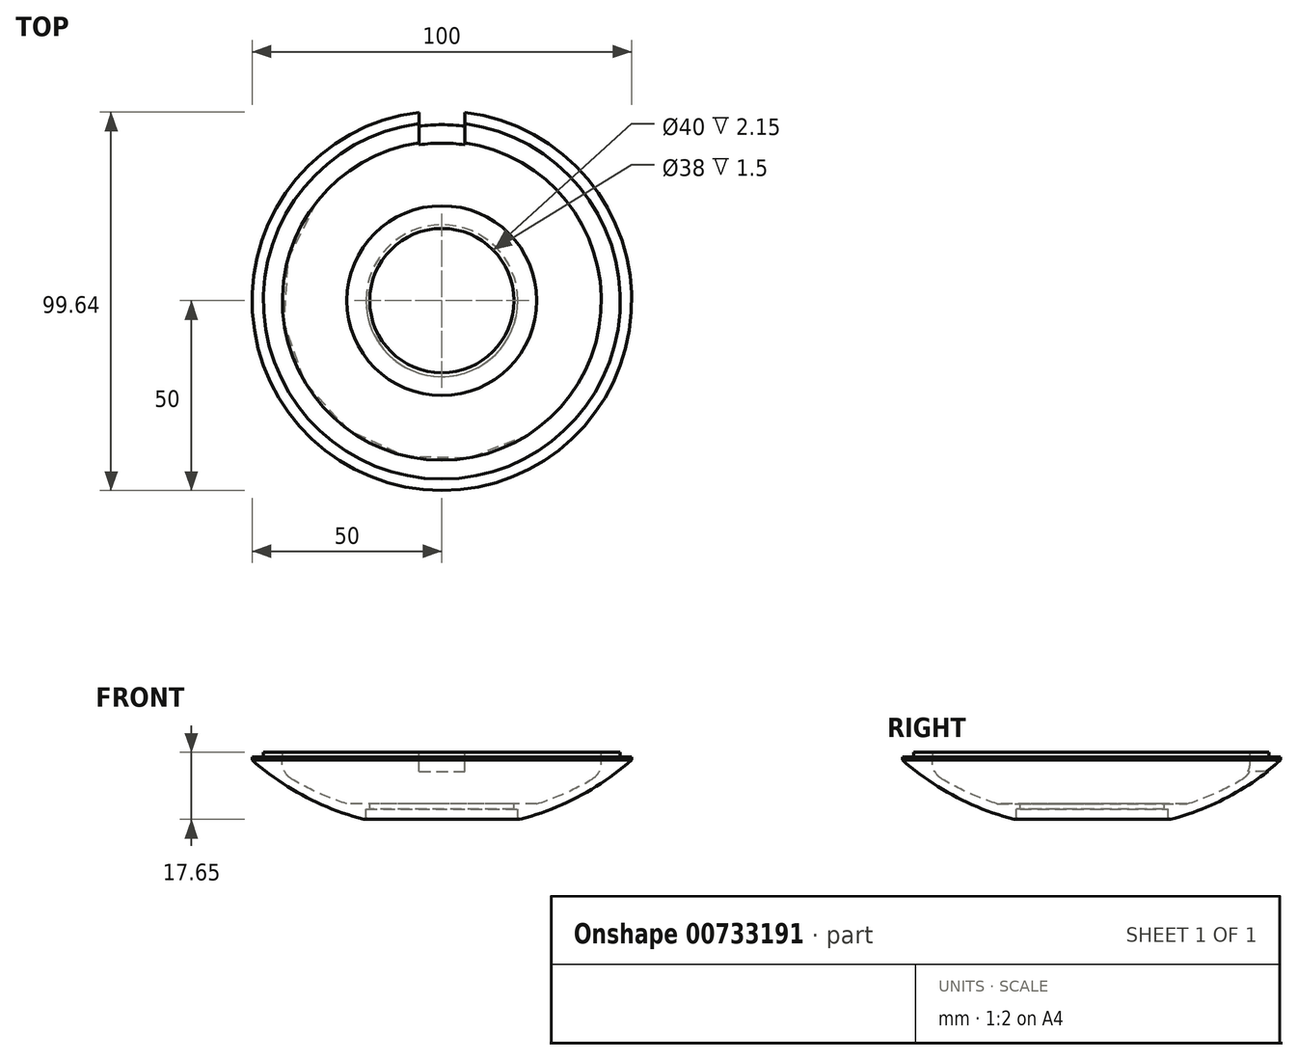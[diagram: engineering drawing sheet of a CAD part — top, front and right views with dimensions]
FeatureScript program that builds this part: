
annotation { "Feature Type Name" : "Feature", "Feature Type Description" : "" }
export const myFeature = defineFeature(function(context is Context, id is Id, definition is map)
    precondition{}
    {
        {
            var Q0;
            Q0=qCreatedBy(makeId("Right.planeOp"),FACE);
            var sketch = newSketch(context, id + "F0", { "sketchPlane" : qUnion([Q0])});
            skArc(sketch, "E0", {"start": v(-47, 0) * mm, "mid": v(-24.82, -11.62) * mm, "end": v(0, -15) * mm});
            skLineSegment(sketch, "E1", {"start": v(-47, 0) * mm, "end": v(-42, 0) * mm});
            skLineSegment(sketch, "E2", {"start": v(-42, 0) * mm, "end": v(-42, 2) * mm});
            skLineSegment(sketch, "E3", {"start": v(-42, 2) * mm, "end": v(-47, 2) * mm});
            skLineSegment(sketch, "E4", {"start": v(-47, 2) * mm, "end": v(-47, 3.7) * mm});
            skLineSegment(sketch, "E5", {"start": v(-47, 3.7) * mm, "end": v(-42, 3.7) * mm});
            skLineSegment(sketch, "E6", {"start": v(-42, 3.7) * mm, "end": v(-42, 5.7) * mm});
            skLineSegment(sketch, "E7", {"start": v(-45, 5.7) * mm, "end": v(-50, 5.7) * mm});
            skLineSegment(sketch, "E8", {"start": v(-50, 5.7) * mm, "end": v(-50, 0) * mm});
            skArc(sketch, "E9", {"start": v(-50, 0) * mm, "mid": v(-26.7, -13.74) * mm, "end": v(0, -18) * mm});
            skLineSegment(sketch, "E10", {"start": v(0, -15) * mm, "end": v(0, -18) * mm});
            skLineSegment(sketch, "E11", {"start": v(0, 0) * mm, "end": v(0, -18) * mm, "construction": true});
            skArc(sketch, "E12", {"start": v(-11, 19.5) * mm, "mid": v(-27.35, 14.5) * mm, "end": v(-42, 5.7) * mm});
            skArc(sketch, "E13", {"start": v(-14, 21.9) * mm, "mid": v(-30.58, 15.86) * mm, "end": v(-45, 5.7) * mm});
            skLineSegment(sketch, "E14", {"start": v(0, 33) * mm, "end": v(0, 36) * mm});
            skArc(sketch, "E15", {"start": v(0, 36) * mm, "mid": v(-9.93, 31.87) * mm, "end": v(-14, 21.9) * mm});
            skArc(sketch, "E16", {"start": v(0, 33) * mm, "mid": v(-7.92, 30.29) * mm, "end": v(-11, 22.5) * mm});
            skLineSegment(sketch, "E17", {"start": v(-11, 22.5) * mm, "end": v(-2.5, 22.5) * mm});
            skLineSegment(sketch, "E18", {"start": v(-11, 19.5) * mm, "end": v(-2.5, 19.5) * mm});
            skLineSegment(sketch, "E19", {"start": v(-2.5, 22.5) * mm, "end": v(-2.5, 19.5) * mm});
            skLineSegment(sketch, "E20", {"start": v(-47, 2) * mm, "end": v(-47, 0.8) * mm});
            skLineSegment(sketch, "E21", {"start": v(-47, 0.8) * mm, "end": v(-50, 0.8) * mm});
            skSolve(sketch);
        }
        {
            var Q0;
            Q0=makeQuery(id+"F0.imprint","IMPRINT",FACE,{"disambiguationData":[TD([[makeQuery(id+"F0.imprint","IMPRINT",EDGE,{"derivedFrom":sQuery(id+"F0.wireOp",EDGE,"E0")}),-1.0]])]});
            var Q1;
            Q1=sQuery(id+"F0.wireOp",EDGE,"E11");
            revolve(context, id + "F1", {"surfaceOperationType" : NewSurfaceOperationType.NEW, "entities" : qUnion([Q0]), "axis" : qUnion([Q1]), "revolveType" : RevolveType.ONE_DIRECTION, "angle" : 360 * degree});
        }
        {
            var Q0;
            Q0=qCreatedBy(makeId("Top.planeOp"),FACE);
            var sketch = newSketch(context, id + "F2", { "sketchPlane" : qUnion([Q0])});
            skCircle(sketch, "E22", {"center": v(0, 0) * mm, "radius": 20 * mm});
            skSolve(sketch);
        }
        {
            var Q0;
            Q0=makeQuery(id+"F2.imprint","IMPRINT",FACE,{"disambiguationData":[TD([[makeQuery(id+"F2.imprint","IMPRINT",EDGE,{"derivedFrom":sQuery(id+"F2.wireOp",EDGE,"E22")}),1.0]])]});
            extrude(context, id + "F3", {"entities" : qUnion([Q0]), "operationType" : NewBodyOperationType.REMOVE, "oppositeDirection" : true, "depth" : 25 * mm, "offsetDistance" : 25 * mm});
        }
        {
            var Q0;
            Q0=qCreatedBy(makeId("Top.planeOp"),FACE);
            var sketch = newSketch(context, id + "F4", { "sketchPlane" : qUnion([Q0])});
            skCircle(sketch, "E23", {"center": v(0, -26) * mm, "radius": 2.5 * mm});
            skCircle(sketch, "E24", {"center": v(-22.52, 13) * mm, "radius": 2.5 * mm});
            skLineSegment(sketch, "E25", {"start": v(0, 0) * mm, "end": v(-22.52, 13) * mm, "construction": true});
            skCircle(sketch, "E26.MirrorC", {"center": v(22.52, 13) * mm, "radius": 2.5 * mm});
            skSolve(sketch);
        }
        {
            var Q0;
            Q0=makeQuery(id+"F4.imprint","IMPRINT",FACE,{"disambiguationData":[TD([[makeQuery(id+"F4.imprint","IMPRINT",EDGE,{"derivedFrom":sQuery(id+"F4.wireOp",EDGE,"E23")}),1.0]])]});
            var Q1;
            Q1=makeQuery(id+"F4.imprint","IMPRINT",FACE,{"disambiguationData":[TD([[makeQuery(id+"F4.imprint","IMPRINT",EDGE,{"derivedFrom":sQuery(id+"F4.wireOp",EDGE,"E24")}),1.0]])]});
            var Q2;
            Q2=makeQuery(id+"F4.imprint","IMPRINT",FACE,{"disambiguationData":[TD([[makeQuery(id+"F4.imprint","IMPRINT",EDGE,{"derivedFrom":sQuery(id+"F4.wireOp",EDGE,"E26.MirrorC")}),-1.0]])]});
            extrude(context, id + "F5", {"entities" : qUnion([Q0, Q1, Q2]), "operationType" : NewBodyOperationType.REMOVE, "depth" : 25 * mm, "offsetDistance" : 25 * mm});
        }
        {
            var Q0;
            Q0=makeQuery(id+"F1.opRevolve","SWEPT_EDGE",EDGE,{"disambiguationData":[OSD([sQuery(id+"F0.wireOp",EDGE,"E0"),sQuery(id+"F0.wireOp",EDGE,"E1")])]});
            var Q1;
            Q1=makeQuery(id+"F1.opRevolve","SWEPT_EDGE",EDGE,{"disambiguationData":[OSD([sQuery(id+"F0.wireOp",EDGE,"E6"),sQuery(id+"F0.wireOp",EDGE,"E12")])]});
            fillet(context, id + "F6", {"entities" : qUnion([Q0, Q1]), "radius" : 5 * mm, "tangentPropagation" : true, "allowEdgeOverflow" : false});
        }
        {
            var Q0;
            Q0=qCreatedBy(makeId("Front.planeOp"),FACE);
            var sketch = newSketch(context, id + "F7", { "sketchPlane" : qUnion([Q0])});
            skLineSegment(sketch, "E27.bottom", {"start": v(-6, 3.6) * mm, "end": v(6, 3.6) * mm});
            skLineSegment(sketch, "E27.top", {"start": v(-6, -3) * mm, "end": v(6, -3) * mm});
            skLineSegment(sketch, "E27.left", {"start": v(-6, 3.6) * mm, "end": v(-6, -3) * mm});
            skLineSegment(sketch, "E27.right", {"start": v(6, 3.6) * mm, "end": v(6, -3) * mm});
            skPoint(sketch, "E28.right.end.orphan", {"position": v(5, 0) * mm});
            skSolve(sketch);
        }
        {
            var Q0;
            Q0=makeQuery(id+"F7.imprint","IMPRINT",FACE,{"disambiguationData":[TD([[makeQuery(id+"F7.imprint","IMPRINT",EDGE,{"derivedFrom":sQuery(id+"F7.wireOp",EDGE,"PHSBLFIY-TZuw-bhm2-DLcI-erlKNIHIbNUr.bottom")}),-1.0]])]});
            var Q1;
            Q1=makeQuery(id+"F7.imprint","IMPRINT",FACE,{"disambiguationData":[TD([[makeQuery(id+"F7.imprint","IMPRINT",EDGE,{"derivedFrom":sQuery(id+"F7.wireOp",EDGE,"PHSBLFIY-TZuw-bhm2-DLcI-erlKNIHIbNUr.right")}),-1.0]])]});
            var Q2;
            Q2=makeQuery(id+"F7.imprint","IMPRINT",FACE,{"disambiguationData":[TD([[makeQuery(id+"F7.imprint","IMPRINT",EDGE,{"derivedFrom":sQuery(id+"F7.wireOp",EDGE,"E27.bottom")}),-1.0]])]});
            extrude(context, id + "F8", {"entities" : qUnion([Q0, Q1, Q2]), "operationType" : NewBodyOperationType.REMOVE, "oppositeDirection" : true, "depth" : 60 * mm, "offsetDistance" : 25 * mm});
        }
        {
            var Q0;
            Q0=qCreatedBy(makeId("Right.planeOp"),FACE);
            var sketch = newSketch(context, id + "F9", { "sketchPlane" : qUnion([Q0])});
            skLineSegment(sketch, "E29.bottom", {"start": v(25, -11.5) * mm, "end": v(19, -11.5) * mm});
            skLineSegment(sketch, "E29.top", {"start": v(25, -13) * mm, "end": v(19, -13) * mm});
            skLineSegment(sketch, "E29.left", {"start": v(25, -11.5) * mm, "end": v(25, -13) * mm});
            skLineSegment(sketch, "E29.right", {"start": v(19, -11.5) * mm, "end": v(19, -13) * mm});
            skLineSegment(sketch, "E30", {"start": v(0, 0) * mm, "end": v(0, -11.57) * mm, "construction": true});
            skSolve(sketch);
        }
        {
            var Q0;
            Q0=makeQuery(id+"F3.boolean.opBoolean","INTERSECT",EDGE,{"derivedFrom":[makeQuery(id+"F1.opRevolve","SWEPT_FACE",FACE,{"disambiguationData":[OSD([sQuery(id+"F0.wireOp",EDGE,"E9")])]}),makeQuery(id+"F3.opExtrude","SWEPT_FACE",FACE,{"disambiguationData":[OSD([sQuery(id+"F2.wireOp",EDGE,"E22")])]})]});
            fillet(context, id + "F10", {"entities" : qUnion([Q0]), "radius" : 0.5 * mm, "tangentPropagation" : true, "allowEdgeOverflow" : false});
        }
        {
            var Q0;
            Q0=makeQuery(id+"F9.imprint","IMPRINT",FACE,{"disambiguationData":[TD([[makeQuery(id+"F9.imprint","IMPRINT",EDGE,{"derivedFrom":sQuery(id+"F9.wireOp",EDGE,"E29.bottom")}),1.0]])]});
            var Q1;
            Q1=sQuery(id+"F9.wireOp",EDGE,"E30");
            revolve(context, id + "F11", {"operationType" : NewBodyOperationType.ADD, "surfaceOperationType" : NewSurfaceOperationType.NEW, "entities" : qUnion([Q0]), "axis" : qUnion([Q1]), "revolveType" : RevolveType.FULL});
        }
    });
